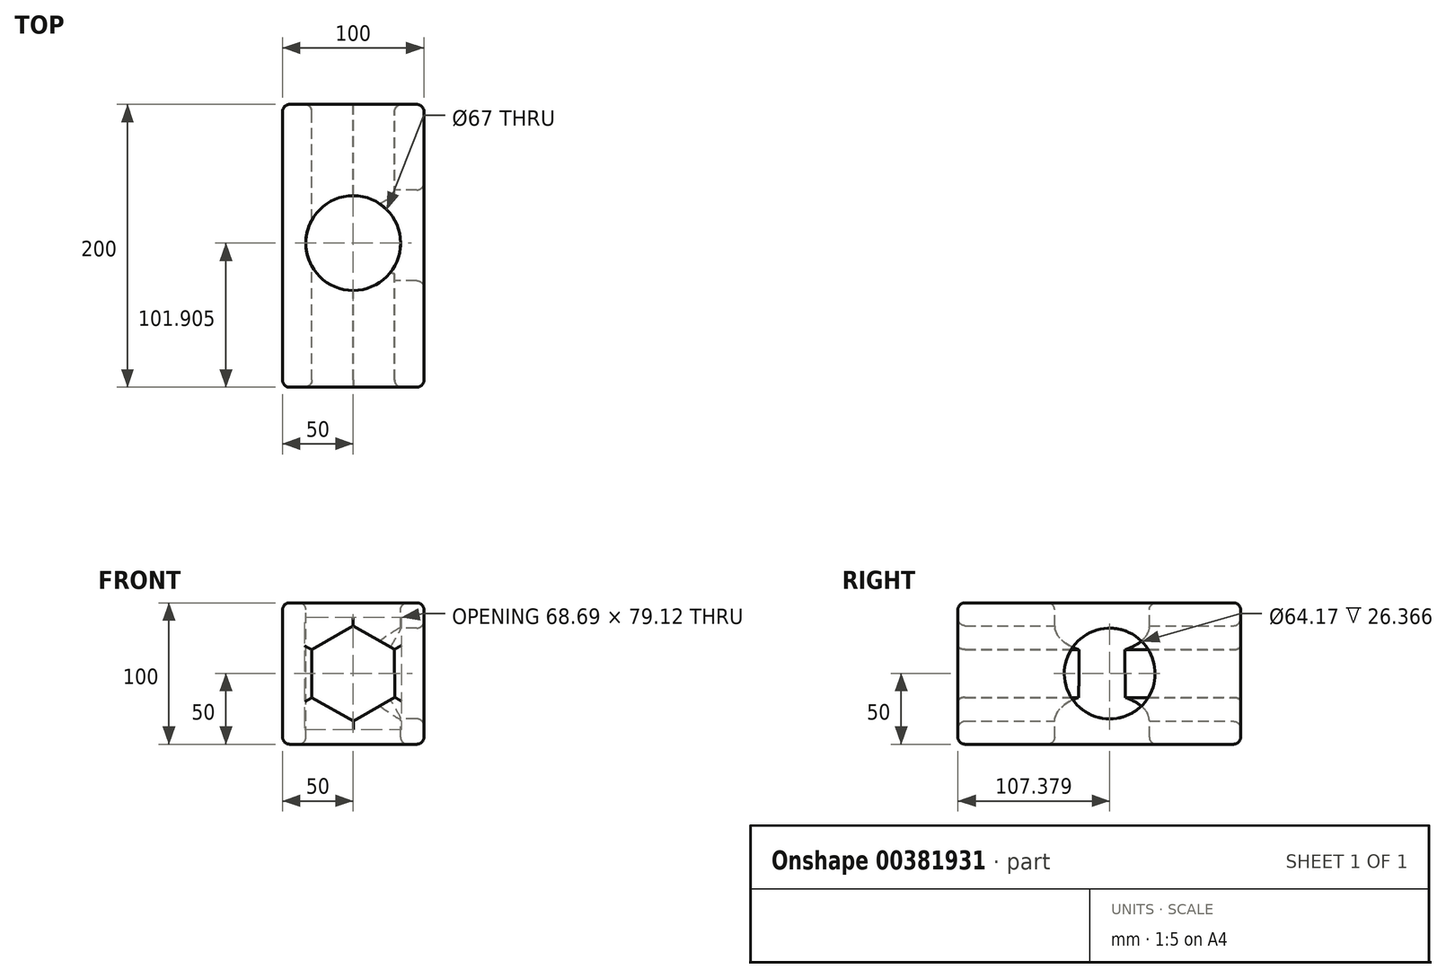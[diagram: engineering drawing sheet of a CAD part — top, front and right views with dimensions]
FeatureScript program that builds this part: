
annotation { "Feature Type Name" : "Feature", "Feature Type Description" : "" }
export const myFeature = defineFeature(function(context is Context, id is Id, definition is map)
    precondition{}
    {
        {
            var Q0;
            Q0=qCreatedBy(makeId("Front.planeOp"),FACE);
            var sketch = newSketch(context, id + "F0", { "sketchPlane" : qUnion([Q0])});
            skLineSegment(sketch, "E0.bottom", {"start": v(50, 50) * mm, "end": v(-50, 50) * mm});
            skLineSegment(sketch, "E0.top", {"start": v(50, -50) * mm, "end": v(-50, -50) * mm});
            skLineSegment(sketch, "E0.left", {"start": v(50, 50) * mm, "end": v(50, -50) * mm});
            skLineSegment(sketch, "E0.right", {"start": v(-50, 50) * mm, "end": v(-50, -50) * mm});
            skPoint(sketch, "E0.middle", {"position": v(0, 0) * mm});
            skCircle(sketch, "E1.cCircle", {"center": v(0, 0) * mm, "radius": 29.26 * mm, "construction": true});
            skLineSegment(sketch, "E1.0", {"start": v(-0.15, 33.78) * mm, "end": v(29.18, 17.02) * mm});
            skLineSegment(sketch, "E1.1", {"start": v(29.18, 17.02) * mm, "end": v(29.33, -16.76) * mm});
            skLineSegment(sketch, "E1.2", {"start": v(29.33, -16.76) * mm, "end": v(0.15, -33.78) * mm});
            skLineSegment(sketch, "E1.3", {"start": v(0.15, -33.78) * mm, "end": v(-29.18, -17.02) * mm});
            skLineSegment(sketch, "E1.4", {"start": v(-29.18, -17.02) * mm, "end": v(-29.33, 16.76) * mm});
            skLineSegment(sketch, "E1.5", {"start": v(-29.33, 16.76) * mm, "end": v(-0.15, 33.78) * mm});
            skPoint(sketch, "E1.0.midPoint", {"position": v(14.52, 25.4) * mm});
            skSolve(sketch);
        }
        {
            var Q0;
            Q0 = qSketchRegion(id + "F0", true);
            extrude(context, id + "F1", {"entities" : qUnion([Q0]), "depth" : 200 * mm});
        }
        {
            var Q0;
            Q0 = qSketchRegion(id + "F0", true);
            extrude(context, id + "F2", {"entities" : qUnion([Q0]), "operationType" : NewBodyOperationType.ADD, "depth" : 25 * mm});
        }
        {
            var Q0;
            Q0=qCreatedBy(makeId("Top.planeOp"),FACE);
            var sketch = newSketch(context, id + "F3", { "sketchPlane" : qUnion([Q0])});
            skCircle(sketch, "E2", {"center": v(2.33, -101.09) * mm, "radius": 27.38 * mm});
            skSolve(sketch);
        }
        {
            var Q0;
            Q0=makeQuery(id+"F3.imprint","IMPRINT",FACE,{"disambiguationData":[TD([[makeQuery(id+"F3.imprint","IMPRINT",EDGE,{"derivedFrom":sQuery(id+"F3.wireOp",EDGE,"E2")}),1.0]])]});
            var Q1;
            Q1=sQuery(id+"F3.wireOp",EDGE,"E2");
            extrude(context, id + "F4", {"entities" : qUnion([Q0]), "operationType" : NewBodyOperationType.REMOVE, "surfaceEntities" : qUnion([Q1]), "oppositeDirection" : true, "depth" : 67 * mm});
        }
        {
            var Q0;
            Q0=makeQuery(id+"F1.opExtrude","SWEPT_FACE",FACE,{"disambiguationData":[OSD([sQuery(id+"F0.wireOp",EDGE,"E0.bottom")])]});
            var sketch = newSketch(context, id + "F5", { "sketchPlane" : qUnion([Q0])});
            skCircle(sketch, "E3", {"center": v(0, -98.1) * mm, "radius": 33.5 * mm});
            skSolve(sketch);
        }
        {
            var Q0;
            Q0 = qSketchRegion(id + "F5", true);
            extrude(context, id + "F6", {"entities" : qUnion([Q0]), "operationType" : NewBodyOperationType.REMOVE, "endBound" : BoundingType.THROUGH_ALL, "oppositeDirection" : true, "depth" : 25 * mm});
        }
        {
            var Q0;
            Q0=qCreatedBy(makeId("Right.planeOp"),FACE);
            var sketch = newSketch(context, id + "F7", { "sketchPlane" : qUnion([Q0])});
            skCircle(sketch, "E4", {"center": v(-92.62, 0) * mm, "radius": 32.08 * mm});
            skSolve(sketch);
        }
        {
            var Q0;
            Q0 = qSketchRegion(id + "F7", true);
            extrude(context, id + "F8", {"entities" : qUnion([Q0]), "operationType" : NewBodyOperationType.REMOVE, "endBound" : BoundingType.THROUGH_ALL, "depth" : 25 * mm});
        }
        {
            var Q0;
            Q0=makeQuery(id+"F1.opExtrude","SWEPT_FACE",FACE,{"disambiguationData":[OSD([sQuery(id+"F0.wireOp",EDGE,"E0.bottom")])]});
            var Q1;
            Q1=makeQuery(id+"F1.opExtrude","SWEPT_FACE",FACE,{"disambiguationData":[OSD([sQuery(id+"F0.wireOp",EDGE,"E0.left")])]});
            fillet(context, id + "F9", {"entities" : qUnion([Q0, Q1]), "radius" : 5 * mm, "tangentPropagation" : true, "allowEdgeOverflow" : false});
        }
        {
            var Q0;
            Q0=makeQuery(id+"F1.opExtrude","CAP_FACE",FACE,{"disambiguationData":[OSD([sQuery(id+"F0.wireOp",EDGE,"E0.bottom"),sQuery(id+"F0.wireOp",EDGE,"E0.top"),sQuery(id+"F0.wireOp",EDGE,"E0.left"),sQuery(id+"F0.wireOp",EDGE,"E0.right"),sQuery(id+"F0.wireOp",EDGE,"E1.0"),sQuery(id+"F0.wireOp",EDGE,"E1.1"),sQuery(id+"F0.wireOp",EDGE,"E1.2"),sQuery(id+"F0.wireOp",EDGE,"E1.3"),sQuery(id+"F0.wireOp",EDGE,"E1.4"),sQuery(id+"F0.wireOp",EDGE,"E1.5")])],"isStart":false});
            fillet(context, id + "F10", {"entities" : qUnion([Q0]), "radius" : 5 * mm, "tangentPropagation" : true, "allowEdgeOverflow" : false});
        }
        {
            var Q0;
            Q0=makeQuery(id+"F1.opExtrude","SWEPT_FACE",FACE,{"disambiguationData":[OSD([sQuery(id+"F0.wireOp",EDGE,"E0.top")])]});
            fillet(context, id + "F11", {"entities" : qUnion([Q0]), "radius" : 5 * mm, "tangentPropagation" : true, "allowEdgeOverflow" : false});
        }
        {
            var Q0;
            Q0=makeQuery(id+"F1.opExtrude","CAP_FACE",FACE,{"disambiguationData":[OSD([sQuery(id+"F0.wireOp",EDGE,"E0.bottom"),sQuery(id+"F0.wireOp",EDGE,"E0.top"),sQuery(id+"F0.wireOp",EDGE,"E0.left"),sQuery(id+"F0.wireOp",EDGE,"E0.right"),sQuery(id+"F0.wireOp",EDGE,"E1.0"),sQuery(id+"F0.wireOp",EDGE,"E1.1"),sQuery(id+"F0.wireOp",EDGE,"E1.2"),sQuery(id+"F0.wireOp",EDGE,"E1.3"),sQuery(id+"F0.wireOp",EDGE,"E1.4"),sQuery(id+"F0.wireOp",EDGE,"E1.5")])],"isStart":true});
            fillet(context, id + "F12", {"entities" : qUnion([Q0]), "radius" : 5 * mm, "tangentPropagation" : true, "allowEdgeOverflow" : false});
        }
    });
